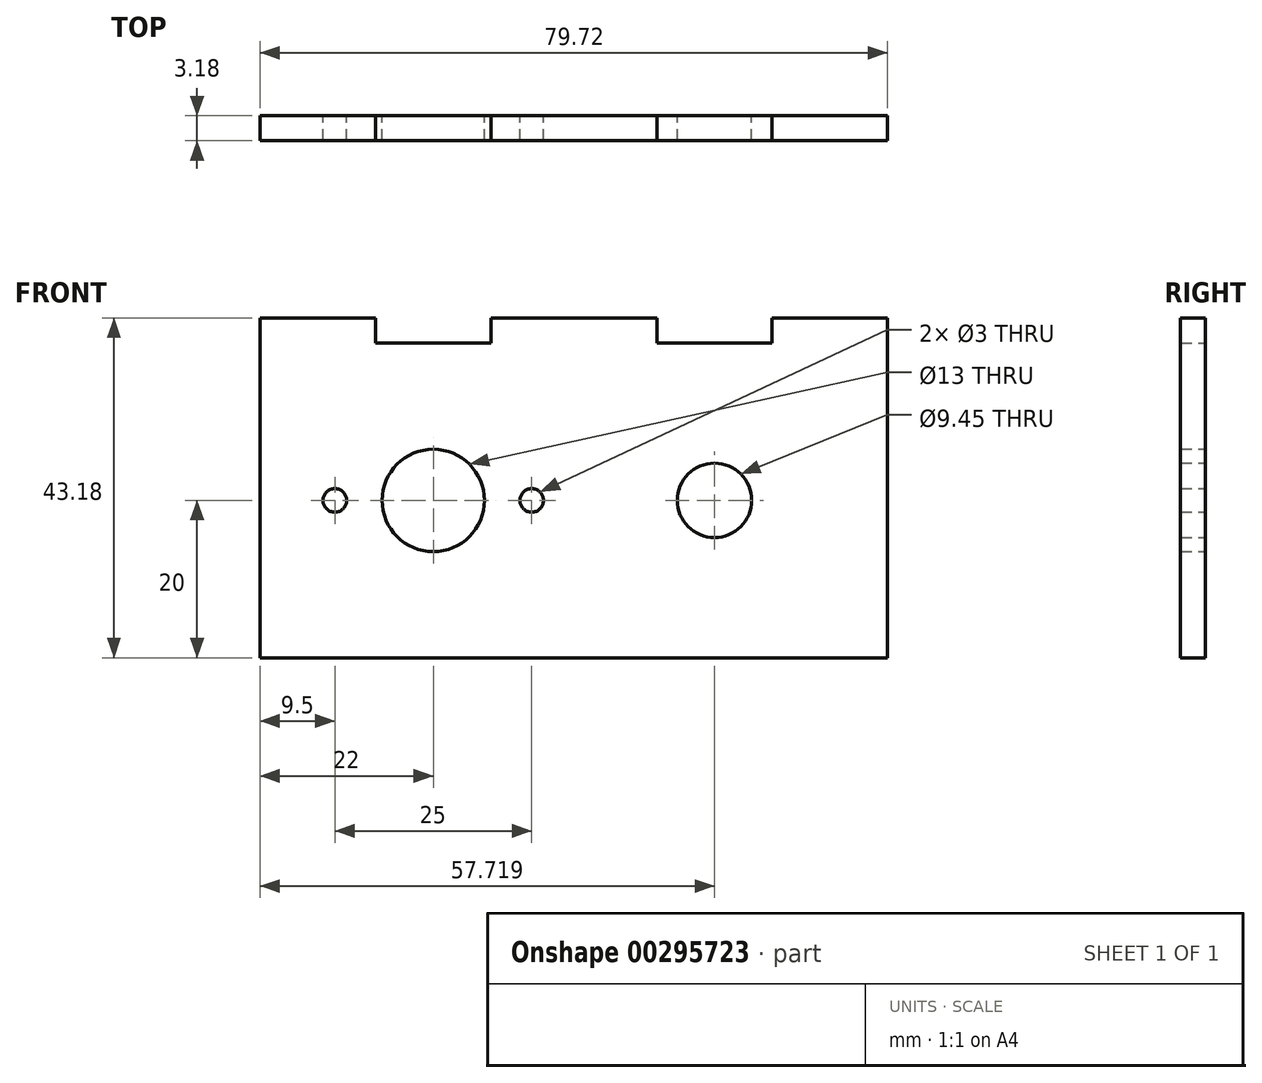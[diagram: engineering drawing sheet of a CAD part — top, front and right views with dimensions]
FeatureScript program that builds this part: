
annotation { "Feature Type Name" : "Feature", "Feature Type Description" : "" }
export const myFeature = defineFeature(function(context is Context, id is Id, definition is map)
    precondition{}
    {
        {
            var Q0;
            Q0=qCreatedBy(makeId("Front.planeOp"),FACE);
            var sketch = newSketch(context, id + "F0", { "sketchPlane" : qUnion([Q0])});
            skCircle(sketch, "E0", {"center": v(0, 0) * mm, "radius": 6.5 * mm});
            skCircle(sketch, "E1", {"center": v(12.5, 0) * mm, "radius": 1.5 * mm});
            skCircle(sketch, "E2.MirrorC", {"center": v(-12.5, 0) * mm, "radius": 1.5 * mm});
            skLineSegment(sketch, "E3.bottom", {"start": v(22, -20) * mm, "end": v(-22, -20) * mm});
            skLineSegment(sketch, "E3.top", {"start": v(22, 20) * mm, "end": v(-22, 20) * mm});
            skLineSegment(sketch, "E3.left", {"start": v(22, -20) * mm, "end": v(22, 20) * mm});
            skLineSegment(sketch, "E3.right", {"start": v(-22, -20) * mm, "end": v(-22, 20) * mm});
            skCircle(sketch, "E4", {"center": v(35.72, 0) * mm, "radius": 4.72 * mm});
            skLineSegment(sketch, "E5.bottom", {"start": v(57.72, -20) * mm, "end": v(13.72, -20) * mm});
            skLineSegment(sketch, "E5.top", {"start": v(57.72, 20) * mm, "end": v(13.72, 20) * mm});
            skLineSegment(sketch, "E5.left", {"start": v(57.72, -20) * mm, "end": v(57.72, 20) * mm});
            skLineSegment(sketch, "E5.right", {"start": v(13.72, -20) * mm, "end": v(13.72, 20) * mm});
            skSolve(sketch);
        }
        {
            var Q0;
            Q0=qSketchRegion(id+"F0",true);
            extrude(context, id + "F1", {"entities" : qUnion([Q0]), "depth" : 3.17 * mm});
        }
        {
            var Q0;
            Q0=makeQuery(id+"F1.opExtrude","SWEPT_FACE",FACE,{"disambiguationData":[OSD([sQuery(id+"F0.wireOp",EDGE,"E3.top")])]});
            var sketch = newSketch(context, id + "F2", { "sketchPlane" : qUnion([Q0])});
            skLineSegment(sketch, "E6.bottom", {"start": v(-22, 0) * mm, "end": v(-22, 0) * mm});
            skLineSegment(sketch, "E6.top", {"start": v(-22, -3.18) * mm, "end": v(-22, -3.18) * mm});
            skLineSegment(sketch, "E6.left", {"start": v(-22, 0) * mm, "end": v(-22, -3.18) * mm});
            skLineSegment(sketch, "E6.right", {"start": v(-22, 0) * mm, "end": v(-22, -3.18) * mm});
            skLineSegment(sketch, "E7.left", {"start": v(-22, -3.18) * mm, "end": v(-22, 0) * mm});
            skLineSegment(sketch, "E7.right", {"start": v(-22, -3.18) * mm, "end": v(-22, 0) * mm});
            skLineSegment(sketch, "E8.bottom", {"start": v(-22, -3.18) * mm, "end": v(-7.33, -3.18) * mm});
            skLineSegment(sketch, "E8.top", {"start": v(-22, 0) * mm, "end": v(-7.33, 0) * mm});
            skLineSegment(sketch, "E8.right", {"start": v(-7.33, -3.18) * mm, "end": v(-7.33, 0) * mm});
            skLineSegment(sketch, "E9.bottom", {"start": v(-7.33, -3.18) * mm, "end": v(7.33, -3.18) * mm});
            skLineSegment(sketch, "E9.top", {"start": v(-7.33, 0) * mm, "end": v(7.33, 0) * mm});
            skLineSegment(sketch, "E9.right", {"start": v(7.33, -3.18) * mm, "end": v(7.33, 0) * mm});
            skLineSegment(sketch, "E10.bottom", {"start": v(7.33, -3.18) * mm, "end": v(28.39, -3.18) * mm});
            skLineSegment(sketch, "E10.top", {"start": v(7.33, 0) * mm, "end": v(28.39, 0) * mm});
            skLineSegment(sketch, "E10.right", {"start": v(28.39, -3.18) * mm, "end": v(28.39, 0) * mm});
            skLineSegment(sketch, "E11.bottom", {"start": v(28.39, -3.18) * mm, "end": v(43.05, -3.18) * mm});
            skLineSegment(sketch, "E11.top", {"start": v(28.39, 0) * mm, "end": v(43.05, 0) * mm});
            skLineSegment(sketch, "E11.right", {"start": v(43.05, -3.18) * mm, "end": v(43.05, 0) * mm});
            skLineSegment(sketch, "E12.bottom", {"start": v(43.05, -3.18) * mm, "end": v(57.72, -3.18) * mm});
            skLineSegment(sketch, "E12.top", {"start": v(43.05, 0) * mm, "end": v(57.72, 0) * mm});
            skLineSegment(sketch, "E12.right", {"start": v(57.72, -3.18) * mm, "end": v(57.72, 0) * mm});
            skSolve(sketch);
        }
        {
            var Q0;
            Q0=makeQuery(id+"F2.imprint","IMPRINT",FACE,{"disambiguationData":[TD([[makeQuery(id+"F2.imprint","IMPRINT",EDGE,{"derivedFrom":sQuery(id+"F2.wireOp",EDGE,"E8.bottom")}),-1.0]])]});
            var Q1;
            Q1=makeQuery(id+"F2.imprint","IMPRINT",FACE,{"disambiguationData":[TD([[makeQuery(id+"F2.imprint","IMPRINT",EDGE,{"derivedFrom":sQuery(id+"F2.wireOp",EDGE,"E12.bottom")}),-1.0]])]});
            var Q2;
            Q2=makeQuery(id+"F2.imprint","IMPRINT",FACE,{"disambiguationData":[TD([[makeQuery(id+"F2.imprint","IMPRINT",EDGE,{"derivedFrom":sQuery(id+"F2.wireOp",EDGE,"E10.bottom")}),-1.0]])]});
            extrude(context, id + "F3", {"entities" : qUnion([Q0, Q1, Q2]), "operationType" : NewBodyOperationType.ADD, "depth" : 3.17 * mm});
        }
    });
